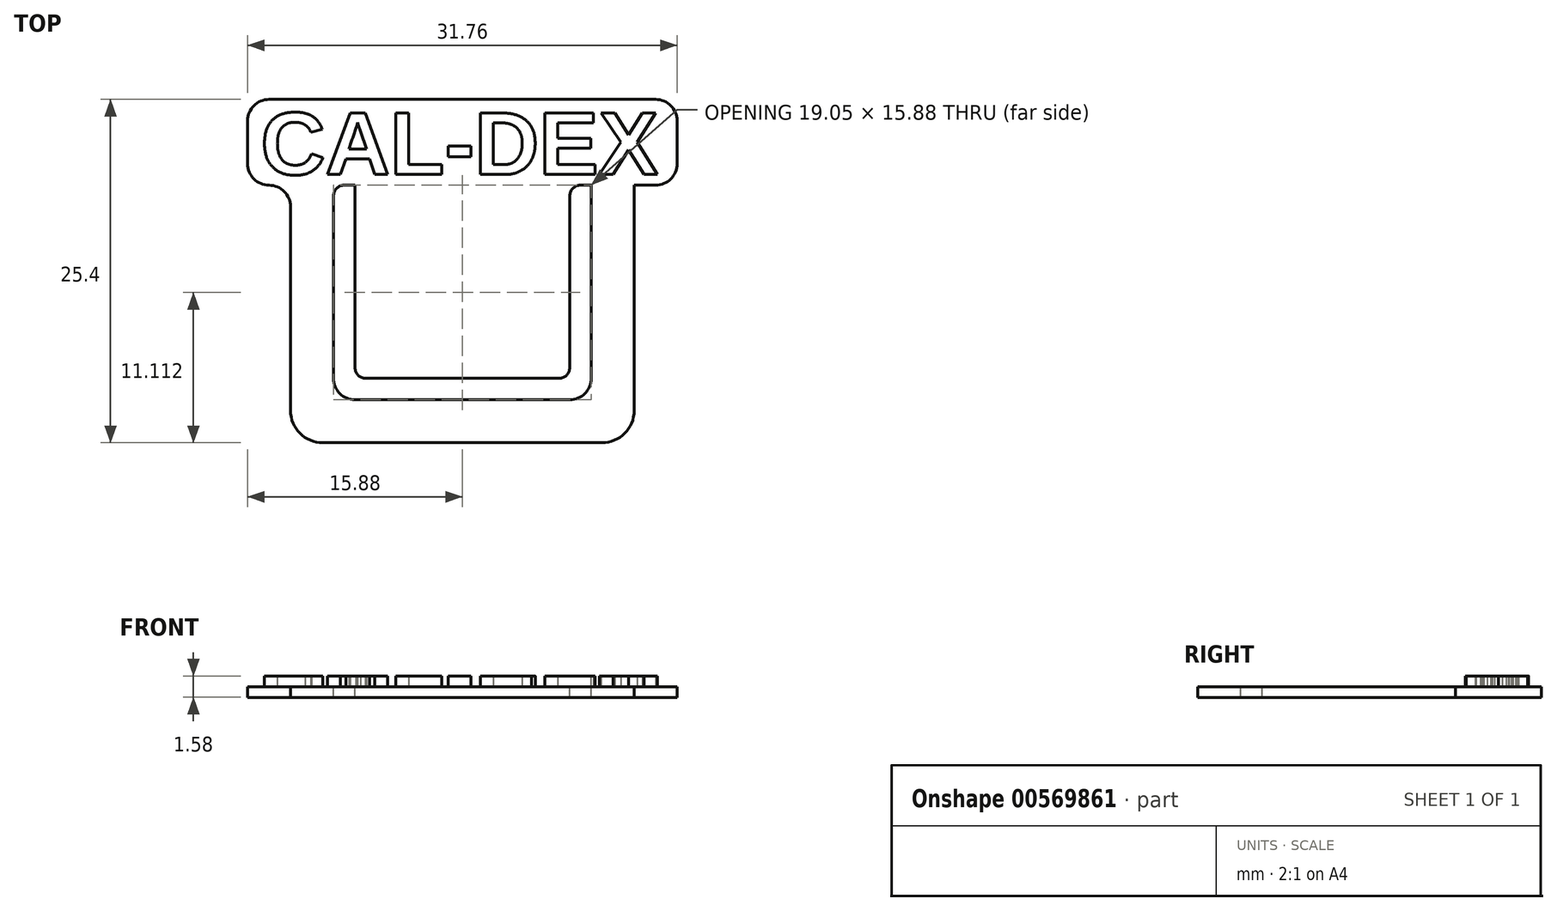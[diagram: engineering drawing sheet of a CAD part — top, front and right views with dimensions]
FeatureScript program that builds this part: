
annotation { "Feature Type Name" : "Feature", "Feature Type Description" : "" }
export const myFeature = defineFeature(function(context is Context, id is Id, definition is map)
    precondition{}
    {
        {
            var Q0;
            Q0=qCreatedBy(makeId("Front.planeOp"),FACE);
            var sketch = newSketch(context, id + "F0", { "sketchPlane" : qUnion([Q0])});
            skLineSegment(sketch, "E0.bottom", {"start": v(12.7, 9.53) * mm, "end": v(-12.7, 9.53) * mm});
            skLineSegment(sketch, "E0.top", {"start": v(12.7, -9.53) * mm, "end": v(-12.7, -9.53) * mm});
            skLineSegment(sketch, "E0.left", {"start": v(12.7, 9.53) * mm, "end": v(12.7, -9.53) * mm});
            skLineSegment(sketch, "E0.right", {"start": v(-12.7, 9.53) * mm, "end": v(-12.7, -9.53) * mm});
            skPoint(sketch, "E0.middle", {"position": v(0, 0) * mm});
            skSolve(sketch);
        }
        {
            var Q0;
            Q0=makeQuery(id+"F0.imprint","IMPRINT",FACE,{"disambiguationData":[TD([[makeQuery(id+"F0.imprint","IMPRINT",EDGE,{"derivedFrom":sQuery(id+"F0.wireOp",EDGE,"E0.bottom")}),1.0]])]});
            extrude(context, id + "F1", {"entities" : qUnion([Q0]), "depth" : 0.8 * mm, "offsetDistance" : 25.4 * mm});
        }
        {
            var Q0;
            Q0=makeQuery(id+"F1.opExtrude","SWEPT_EDGE",EDGE,{"disambiguationData":[OSD([sQuery(id+"F0.wireOp",EDGE,"E0.top"),sQuery(id+"F0.wireOp",EDGE,"E0.left")])]});
            var Q1;
            Q1=makeQuery(id+"F1.opExtrude","SWEPT_EDGE",EDGE,{"disambiguationData":[OSD([sQuery(id+"F0.wireOp",EDGE,"E0.top"),sQuery(id+"F0.wireOp",EDGE,"E0.right")])]});
            fillet(context, id + "F2", {"entities" : qUnion([Q0, Q1]), "radius" : 2.38 * mm, "tangentPropagation" : true, "allowEdgeOverflow" : false});
        }
        {
            var Q0;
            Q0=makeQuery(id+"F1.opExtrude","CAP_FACE",FACE,{"disambiguationData":[OSD([sQuery(id+"F0.wireOp",EDGE,"E0.bottom"),sQuery(id+"F0.wireOp",EDGE,"E0.top"),sQuery(id+"F0.wireOp",EDGE,"E0.left"),sQuery(id+"F0.wireOp",EDGE,"E0.right")])],"isStart":false});
            var sketch = newSketch(context, id + "F3", { "sketchPlane" : qUnion([Q0])});
            skLineSegment(sketch, "E1.bottom", {"start": v(9.52, 9.53) * mm, "end": v(-9.53, 9.53) * mm});
            skLineSegment(sketch, "E1.top", {"start": v(9.53, -6.35) * mm, "end": v(-9.53, -6.35) * mm});
            skLineSegment(sketch, "E1.left", {"start": v(9.52, 9.53) * mm, "end": v(9.53, -6.35) * mm});
            skLineSegment(sketch, "E1.right", {"start": v(-9.53, 9.53) * mm, "end": v(-9.52, -6.35) * mm});
            skPoint(sketch, "E1.middle", {"position": v(0, 0) * mm});
            skSolve(sketch);
        }
        {
            var Q0;
            Q0=makeQuery(id+"F3.imprint","IMPRINT",FACE,{"disambiguationData":[TD([[makeQuery(id+"F3.imprint","IMPRINT",EDGE,{"derivedFrom":sQuery(id+"F3.wireOp",EDGE,"E1.bottom")}),1.0]])]});
            extrude(context, id + "F4", {"entities" : qUnion([Q0]), "operationType" : NewBodyOperationType.REMOVE, "oppositeDirection" : true, "depth" : 4.93 * mm, "offsetDistance" : 25.4 * mm});
        }
        {
            var Q0;
            Q0=makeQuery(id+"F1.opExtrude","CAP_FACE",FACE,{"disambiguationData":[OSD([sQuery(id+"F0.wireOp",EDGE,"E0.bottom"),sQuery(id+"F0.wireOp",EDGE,"E0.top"),sQuery(id+"F0.wireOp",EDGE,"E0.left"),sQuery(id+"F0.wireOp",EDGE,"E0.right")])],"isStart":false});
            var sketch = newSketch(context, id + "F5", { "sketchPlane" : qUnion([Q0])});
            skLineSegment(sketch, "E2.bottom", {"start": v(-15.88, 9.53) * mm, "end": v(15.87, 9.53) * mm});
            skLineSegment(sketch, "E2.top", {"start": v(-15.88, 15.88) * mm, "end": v(15.87, 15.88) * mm});
            skLineSegment(sketch, "E2.left", {"start": v(-15.88, 9.53) * mm, "end": v(-15.88, 15.88) * mm});
            skLineSegment(sketch, "E2.right", {"start": v(15.87, 9.53) * mm, "end": v(15.87, 15.88) * mm});
            skSolve(sketch);
        }
        {
            var Q0;
            Q0=makeQuery(id+"F5.imprint","IMPRINT",FACE,{"disambiguationData":[TD([[makeQuery(id+"F5.imprint","IMPRINT",EDGE,{"derivedFrom":sQuery(id+"F5.wireOp",EDGE,"E2.top")}),-1.0]])]});
            extrude(context, id + "F6", {"entities" : qUnion([Q0]), "operationType" : NewBodyOperationType.ADD, "oppositeDirection" : true, "depth" : 0.8 * mm, "offsetDistance" : 25.4 * mm});
        }
        {
            var Q0;
            Q0=makeQuery(id+"F6.opExtrude","SWEPT_EDGE",EDGE,{"disambiguationData":[OSD([sQuery(id+"F5.wireOp",EDGE,"E2.top"),sQuery(id+"F5.wireOp",EDGE,"E2.left")])]});
            var Q1;
            Q1=makeQuery(id+"F6.opExtrude","SWEPT_EDGE",EDGE,{"disambiguationData":[OSD([sQuery(id+"F5.wireOp",EDGE,"E2.top"),sQuery(id+"F5.wireOp",EDGE,"E2.right")])]});
            var Q2;
            Q2=makeQuery(id+"F6.opExtrude","SWEPT_EDGE",EDGE,{"disambiguationData":[OSD([sQuery(id+"F5.wireOp",EDGE,"E2.bottom"),sQuery(id+"F5.wireOp",EDGE,"E2.right")])]});
            var Q3;
            Q3=makeQuery(id+"F1.opExtrude","SWEPT_EDGE",EDGE,{"disambiguationData":[OSD([sQuery(id+"F0.wireOp",EDGE,"E0.bottom"),sQuery(id+"F0.wireOp",EDGE,"E0.left")])]});
            var Q4;
            Q4=makeQuery(id+"F6.opExtrude","SWEPT_EDGE",EDGE,{"disambiguationData":[OSD([sQuery(id+"F5.wireOp",EDGE,"E2.bottom"),sQuery(id+"F5.wireOp",EDGE,"E2.left")])]});
            var Q5;
            Q5=makeQuery(id+"F1.opExtrude","SWEPT_EDGE",EDGE,{"disambiguationData":[OSD([sQuery(id+"F0.wireOp",EDGE,"E0.bottom"),sQuery(id+"F0.wireOp",EDGE,"E0.right")])]});
            fillet(context, id + "F7", {"entities" : qUnion([Q0, Q1, Q2, Q3, Q4, Q5]), "radius" : 1.59 * mm, "tangentPropagation" : true, "allowEdgeOverflow" : false});
        }
        {
            var Q0;
            Q0=makeQuery(id+"F4.boolean.opBoolean","COPY",EDGE,{"derivedFrom":makeQuery(id+"F4.opExtrude","SWEPT_EDGE",EDGE,{"disambiguationData":[OSD([sQuery(id+"F3.wireOp",EDGE,"E1.top"),sQuery(id+"F3.wireOp",EDGE,"E1.right")])]})});
            var Q1;
            Q1=makeQuery(id+"F4.boolean.opBoolean","COPY",EDGE,{"derivedFrom":makeQuery(id+"F4.opExtrude","SWEPT_EDGE",EDGE,{"disambiguationData":[OSD([sQuery(id+"F3.wireOp",EDGE,"E1.top"),sQuery(id+"F3.wireOp",EDGE,"E1.left")])]})});
            fillet(context, id + "F8", {"entities" : qUnion([Q0, Q1]), "radius" : 1.59 * mm, "tangentPropagation" : true, "allowEdgeOverflow" : false});
        }
        {
            var Q0;
            Q0=makeQuery(id+"F6.boolean.opBoolean","MERGE",FACE,{"derivedFrom":[makeQuery(id+"F1.opExtrude","CAP_FACE",FACE,{"disambiguationData":[OSD([sQuery(id+"F0.wireOp",EDGE,"E0.bottom"),sQuery(id+"F0.wireOp",EDGE,"E0.top"),sQuery(id+"F0.wireOp",EDGE,"E0.left"),sQuery(id+"F0.wireOp",EDGE,"E0.right")])],"isStart":false}),makeQuery(id+"F6.opExtrude","CAP_FACE",FACE,{"disambiguationData":[OSD([sQuery(id+"F5.wireOp",EDGE,"E2.bottom"),sQuery(id+"F5.wireOp",EDGE,"E2.top"),sQuery(id+"F5.wireOp",EDGE,"E2.left"),sQuery(id+"F5.wireOp",EDGE,"E2.right")])],"isStart":true})]});
            var sketch = newSketch(context, id + "F9", { "sketchPlane" : qUnion([Q0])});
            skLineSegment(sketch, "E3.bottom", {"start": v(-7.94, 9.53) * mm, "end": v(7.94, 9.53) * mm});
            skLineSegment(sketch, "E3.top", {"start": v(-7.94, -4.76) * mm, "end": v(7.94, -4.76) * mm});
            skLineSegment(sketch, "E3.left", {"start": v(-7.94, 9.53) * mm, "end": v(-7.94, -4.76) * mm});
            skLineSegment(sketch, "E3.right", {"start": v(7.94, 9.53) * mm, "end": v(7.94, -4.76) * mm});
            skSolve(sketch);
        }
        {
            var Q0;
            Q0=makeQuery(id+"F9.imprint","IMPRINT",FACE,{"disambiguationData":[TD([[makeQuery(id+"F9.imprint","IMPRINT",EDGE,{"derivedFrom":sQuery(id+"F9.wireOp",EDGE,"E3.bottom")}),1.0]])]});
            extrude(context, id + "F10", {"entities" : qUnion([Q0]), "operationType" : NewBodyOperationType.ADD, "oppositeDirection" : true, "depth" : 0.8 * mm, "offsetDistance" : 25.4 * mm});
        }
        {
            var Q0;
            Q0=makeQuery(id+"F10.boolean.opBoolean","MERGE",FACE,{"derivedFrom":[makeQuery(id+"F6.boolean.opBoolean","MERGE",FACE,{"derivedFrom":[makeQuery(id+"F1.opExtrude","CAP_FACE",FACE,{"disambiguationData":[OSD([sQuery(id+"F0.wireOp",EDGE,"E0.bottom"),sQuery(id+"F0.wireOp",EDGE,"E0.top"),sQuery(id+"F0.wireOp",EDGE,"E0.left"),sQuery(id+"F0.wireOp",EDGE,"E0.right")])],"isStart":false}),makeQuery(id+"F6.opExtrude","CAP_FACE",FACE,{"disambiguationData":[OSD([sQuery(id+"F5.wireOp",EDGE,"E2.bottom"),sQuery(id+"F5.wireOp",EDGE,"E2.top"),sQuery(id+"F5.wireOp",EDGE,"E2.left"),sQuery(id+"F5.wireOp",EDGE,"E2.right")])],"isStart":true})]}),makeQuery(id+"F10.opExtrude","CAP_FACE",FACE,{"disambiguationData":[OSD([sQuery(id+"F9.wireOp",EDGE,"E3.bottom"),sQuery(id+"F9.wireOp",EDGE,"E3.top"),sQuery(id+"F9.wireOp",EDGE,"E3.left"),sQuery(id+"F9.wireOp",EDGE,"E3.right")])],"isStart":true})]});
            var sketch = newSketch(context, id + "F11", { "sketchPlane" : qUnion([Q0])});
            skText(sketch, "E4", { "text": "CAL-DEX", "fontName": "Arimo-Bold.ttf"});
            const initialGuessF11  = {"E4": [-0.0149, 0.01032, 1, 0, 0.00476]};
            skSetInitialGuess(sketch, initialGuessF11);
            skSolve(sketch);
        }
        {
            var Q0;
            Q0=qSketchRegion(id+"F11",true);
            extrude(context, id + "F12", {"entities" : qUnion([Q0]), "operationType" : NewBodyOperationType.ADD, "depth" : 0.8 * mm, "offsetDistance" : 25.4 * mm});
        }
        {
            var Q0;
            Q0=makeQuery(id+"F10.opExtrude","SWEPT_EDGE",EDGE,{"disambiguationData":[OSD([sQuery(id+"F5.wireOp",EDGE,"E2.bottom"),sQuery(id+"F9.wireOp",EDGE,"E3.bottom"),sQuery(id+"F9.wireOp",EDGE,"E3.left")])]});
            var Q1;
            Q1=makeQuery(id+"F4.boolean.opBoolean","COPY",EDGE,{"derivedFrom":makeQuery(id+"F4.opExtrude","SWEPT_EDGE",EDGE,{"disambiguationData":[OSD([sQuery(id+"F0.wireOp",EDGE,"E0.bottom"),sQuery(id+"F3.wireOp",EDGE,"E1.bottom"),sQuery(id+"F3.wireOp",EDGE,"E1.right")])]})});
            var Q2;
            Q2=makeQuery(id+"F10.opExtrude","SWEPT_EDGE",EDGE,{"disambiguationData":[OSD([sQuery(id+"F5.wireOp",EDGE,"E2.bottom"),sQuery(id+"F9.wireOp",EDGE,"E3.bottom"),sQuery(id+"F9.wireOp",EDGE,"E3.right")])]});
            var Q3;
            Q3=makeQuery(id+"F4.boolean.opBoolean","COPY",EDGE,{"derivedFrom":makeQuery(id+"F4.opExtrude","SWEPT_EDGE",EDGE,{"disambiguationData":[OSD([sQuery(id+"F0.wireOp",EDGE,"E0.bottom"),sQuery(id+"F3.wireOp",EDGE,"E1.bottom"),sQuery(id+"F3.wireOp",EDGE,"E1.left")])]})});
            fillet(context, id + "F13", {"entities" : qUnion([Q0, Q1, Q2, Q3]), "radius" : 0.8 * mm, "tangentPropagation" : true, "allowEdgeOverflow" : false});
        }
        {
            var Q0;
            Q0=makeQuery(id+"F10.opExtrude","SWEPT_EDGE",EDGE,{"disambiguationData":[OSD([sQuery(id+"F9.wireOp",EDGE,"E3.top"),sQuery(id+"F9.wireOp",EDGE,"E3.left")])]});
            var Q1;
            Q1=makeQuery(id+"F10.opExtrude","SWEPT_EDGE",EDGE,{"disambiguationData":[OSD([sQuery(id+"F9.wireOp",EDGE,"E3.top"),sQuery(id+"F9.wireOp",EDGE,"E3.right")])]});
            fillet(context, id + "F14", {"entities" : qUnion([Q0, Q1]), "radius" : 0.8 * mm, "tangentPropagation" : true, "allowEdgeOverflow" : false});
        }
        {
            var Q0;
            Q0=makeQuery(id+"F1.opExtrude","SWEPT_BODY",BODY,{"disambiguationData":[OSD([sQuery(id+"F0.wireOp",EDGE,"E0.bottom"),sQuery(id+"F0.wireOp",EDGE,"E0.top"),sQuery(id+"F0.wireOp",EDGE,"E0.left"),sQuery(id+"F0.wireOp",EDGE,"E0.right")])]});
            var Q1;
            Q1=makeQuery(id+"F6.opExtrude","CAP_EDGE",EDGE,{"disambiguationData":[OSD([sQuery(id+"F5.wireOp",EDGE,"E2.top")])],"isStart":false});
            transform(context, id + "F15", {"entities" : qUnion([Q0]), "transformType" : TransformType.ROTATION, "transformAxis" : qUnion([Q1]), "angle" : 270 * degree, "makeCopy" : false});
        }
    });
